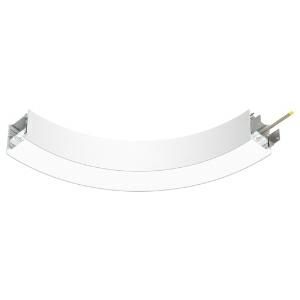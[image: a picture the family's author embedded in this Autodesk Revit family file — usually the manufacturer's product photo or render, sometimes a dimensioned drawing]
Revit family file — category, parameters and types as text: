
# Revit family: super-g_slim_super_g_slim_dir_ind_800_90deg_hl_ps_led_18w__2880lm__3000k__cri80_430-3710_0258
name_source: partatom
category: Leuchten
revit_build: Autodesk Revit 2016 (Build: 20190508_0715(x64)
units: mm (PartAtom-declared; Revit-internal decimal feet)

## family parameters
Basisbauteil = Fläche
Beim Laden mit Abzugskörper schneiden = Nein
Bemaßung runder Anschluss = Durchmesser verwenden
Gemeinsam genutzt = Nein
Lichtquelle = Nein
Raumberechnungspunkt = Nein
Teiletyp = Normal

## types (1)
- 430-3710-D01 (1 x LED, 720 lm, 3000K)
    Beschreibung = The insert consists of aluminum-extruded profile. Charming SOFT-EDGE design ensure unparalleled styling. The ballast is integrated and allows for an operation with 220-240V (50/60Hz). SUPER-G SLIM (# 430-3710) ist not dimmable (on/off).
    CIE Flux Codes = 48 79 96 66 85
    Color Rendering = 1B/80…89
    Color Temperature = 3000K
    Height = 90 mm
    Hersteller = Prolicht
    Lamp Light Flux = 720 lm
    Lamp count = 1
    Lampe = 1 x LED
    Length = 144 mm
    Luminous efficacy = 122 lm/W
    ModVariant = Nein
    Modell = 430-3710
    Mounting Place = Ceiling
    Mounting Type = Pendant
    Number of Poles = 1
    OnlyDefault = Ja
    Power Factor = 1
    Product Name = SUPER-G SLIM__SUPER G SLIM DIR/IND 800/90° HL PS LED 18W  2880lm  3000K  CRI80
    Product group = Suspended profile systems
    ProductGroupID = 944
    Protection Class = Protection class
    Protection Degree = Degree of protection
    RLX_Detail_Level = 1
    RlxData = <blob elided: 38173 chars, md5=ba9c5192>
    Scheinlast = 20 VA
    Socket = socket
    Standby Power = 0 W
    System Light Flux = 2436 lm
    System Power = 20 W
    Typenbild = 430-3710.jpg
    URL = http://relux.com
    VarID = 430-3710-d01
    Voltage = 0 V
    Vorgabe-Ansicht = 1800 mm
    Weight = 0.00 kg
    Width = 65 mm

## geometry (parser evidence)
native form markers: Sweep x31
no freeform markers — native parametric forms only
